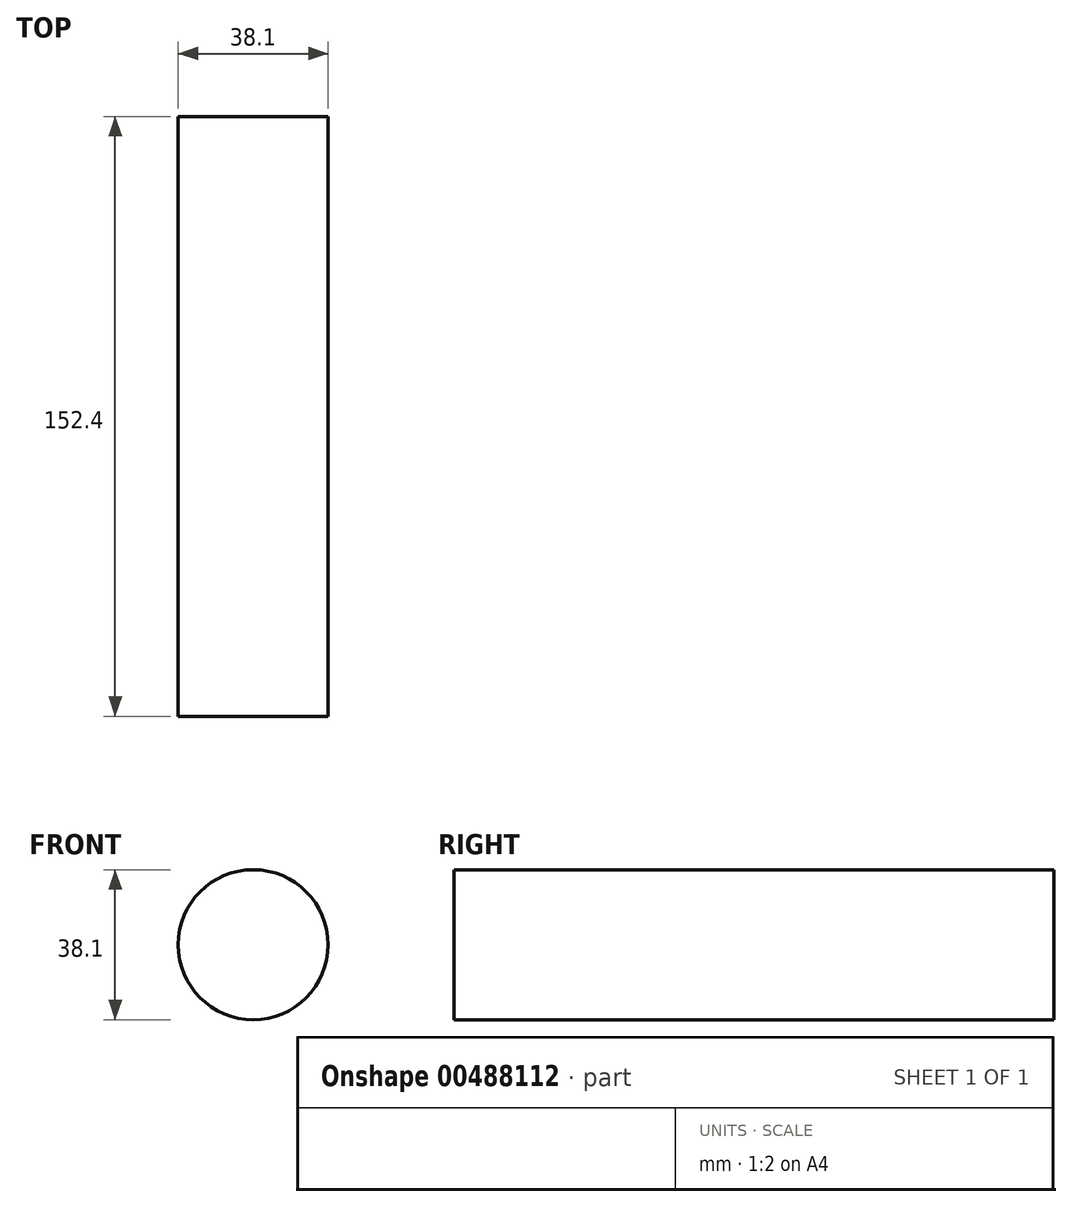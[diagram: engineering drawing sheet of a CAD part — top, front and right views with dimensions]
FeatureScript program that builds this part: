
annotation { "Feature Type Name" : "Feature", "Feature Type Description" : "" }
export const myFeature = defineFeature(function(context is Context, id is Id, definition is map)
    precondition{}
    {
        {
            var Q0;
            Q0=qCreatedBy(makeId("Front.planeOp"),FACE);
            var sketch = newSketch(context, id + "F0", { "sketchPlane" : qUnion([Q0])});
            skCircle(sketch, "E0", {"center": v(0, 0) * mm, "radius": 19.05 * mm});
            skSolve(sketch);
        }
        {
            var Q0;
            Q0=makeQuery(id+"F0.imprint","IMPRINT",FACE,{"disambiguationData":[TD([[makeQuery(id+"F0.imprint","IMPRINT",EDGE,{"derivedFrom":sQuery(id+"F0.wireOp",EDGE,"E0")}),1.0]])]});
            extrude(context, id + "F1", {"entities" : qUnion([Q0]), "depth" : 152.4 * mm, "offsetDistance" : 25.4 * mm});
        }
    });
